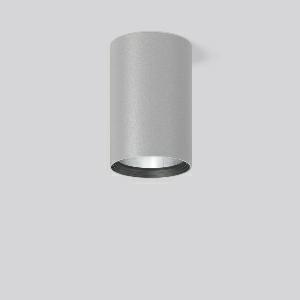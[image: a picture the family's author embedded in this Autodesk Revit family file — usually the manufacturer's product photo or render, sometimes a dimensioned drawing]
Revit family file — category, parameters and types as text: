
# Revit family: heledon_maxi_a_931237_004_76_4232
name_source: partatom
category: Lighting Fixtures
units: mm (PartAtom-declared; Revit-internal decimal feet)

## family parameters
Cut with Voids When Loaded = No
Host = Face
Light Source = No
Part Type = Normal
Room Calculation Point = No
Round Connector Dimension = Use Diameter
Shared = No

## types (1)
- HELEDON maxi A (1 x LED Modul 920 meat+, 2200 lm, 2000)
    Apparent Load = 33 VA
    Approval mark = CE
    CIE Flux Codes = 100 100 100 100 100
    Color Rendering = 90
    Color Temperature = 2000
    Default Elevation = 1800 mm
    Description = Series: HELEDON maxi
Cylindrical surface-mounted downlight. Housing: die-cast aluminium, powder-coated. Internal ceiling frame polycarbonate with bayonet mounting. Black plastic ring and recessed LED to prevent glare from the side. Optical assembly with reflector made of MIRO-Silver with 98% total light reflection for outstanding efficiency - can be changed without tools. Special LED for illumination of meat included. Suitable for Ceiling mounting. Easy installation with a separate ceiling frame with bayonet mounting and plug connection. Driver integrated. Connected via plug-in connector. High quality converter without flickering and stroboscopic effect. The following accessories can be mounted without use of tools: interchangeable lenses, decorative glasses, honeycomb louvre, clear and frosted diffusers, white interchangeable plastic ring. 
Colour: silver
Diameter: 123 mm
Height: 183 mm
Lamp: LED
Socket: without socket
Colour temperature: meat +
System power: 33 W
Rated luminous flux: 2200 lm
Luminous efficiency: 67 lm/W
Control gear: Converter, dimmable, DALI
Protection class: I
Type of protection: IP 20
    Height = 183 mm
    Lamp = 1 x LED Modul 920 meat+
    Lamp Light Flux = 2200 lm
    Lamp count = 1
    Length = 123 mm
    Lifetime = 50000 h
    Luminous efficacy = 67 lm/W
    Manufacturer = RZB
    ModVariant = No
    Model = 931237.004.76
    Mounting Place = Ceiling
    Mounting Type = Surface mounted
    Number of Poles = 1
    OnlyDefault = Yes
    Power Factor = 1
    Product Name = HELEDON maxi A
    Product group = Surface mounted downlights
    ProductGroupID = 302
    Protection Class = Protection class I
    Protection Degree = IP 20
    RLX_Detail_Level = 1
    RLX_Emergency_Light_Flux = 0 lm
    RLX_Emergency_Type = 0
    RLX_Emergency_Type_DB = No
    RlxData = <blob elided: 98201 chars, md5=7b9bbae2>
    Socket = socket
    Standby Power = 0 W
    System Light Flux = 2200 lm
    System Power = 33 W
    Type Comments = Product without accessories
    Type Image = 931192.004.jpg
    URL = http://relux.com
    VarID = ---
    Voltage = 230 V
    Voltage Range = 220-240 V
    Weight = 0.00 kg
    Width = 0 mm  [stored 0 ft]

note: [stored X ft] marks values corroborated as IEEE doubles in the binary element streams (Revit-internal decimal feet)

## geometry (parser evidence)
native form markers: Blend x4, Sweep x10
no freeform markers — native parametric forms only
